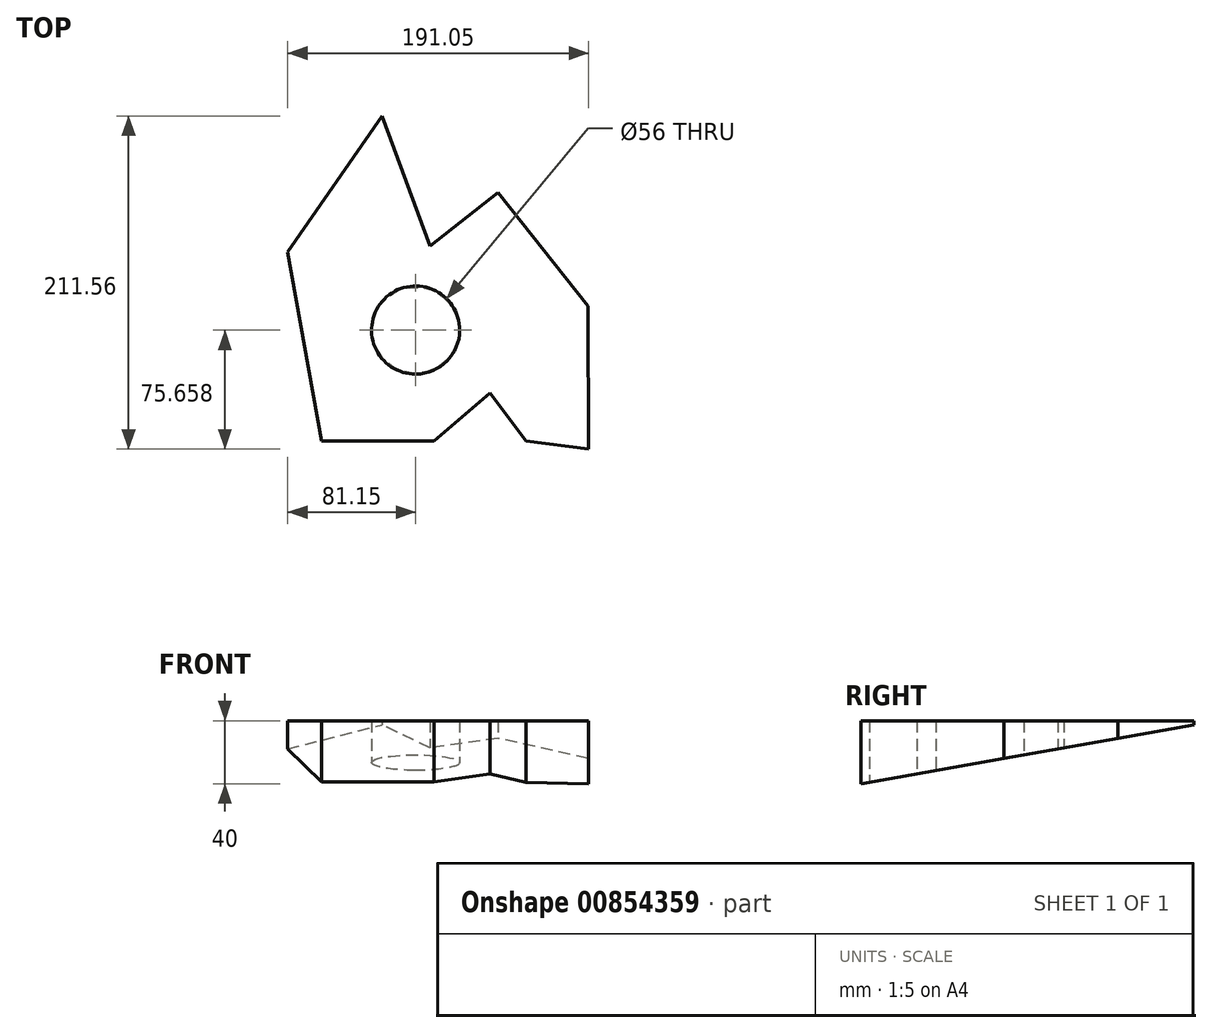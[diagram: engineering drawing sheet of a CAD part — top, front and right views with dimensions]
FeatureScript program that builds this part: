
annotation { "Feature Type Name" : "Feature", "Feature Type Description" : "" }
export const myFeature = defineFeature(function(context is Context, id is Id, definition is map)
    precondition{}
    {
        {
            var Q0;
            Q0=qCreatedBy(makeId("Top.planeOp"),FACE);
            var sketch = newSketch(context, id + "F0", { "sketchPlane" : qUnion([Q0])});
            skLineSegment(sketch, "E0", {"start": v(-21.43, 120.56) * mm, "end": v(-81.15, 34.2) * mm});
            skLineSegment(sketch, "E1", {"start": v(-21.43, 120.56) * mm, "end": v(9.15, 38.05) * mm});
            skLineSegment(sketch, "E2", {"start": v(9.15, 38.05) * mm, "end": v(52.3, 72.16) * mm});
            skLineSegment(sketch, "E3", {"start": v(52.3, 72.16) * mm, "end": v(109.36, 0) * mm});
            skLineSegment(sketch, "E4", {"start": v(109.36, 0) * mm, "end": v(109.9, -91) * mm});
            skLineSegment(sketch, "E5", {"start": v(109.9, -91) * mm, "end": v(70.25, -85.66) * mm});
            skLineSegment(sketch, "E6", {"start": v(70.25, -85.66) * mm, "end": v(47.2, -55.46) * mm});
            skLineSegment(sketch, "E7", {"start": v(47.2, -119.83) * mm, "end": v(-59.8, -119.83) * mm});
            skLineSegment(sketch, "E8", {"start": v(47.2, -55.46) * mm, "end": v(-5.77, -100.48) * mm});
            skLineSegment(sketch, "E9", {"start": v(11.65, -85.66) * mm, "end": v(-59.8, -85.66) * mm});
            skLineSegment(sketch, "E10", {"start": v(-59.8, -85.66) * mm, "end": v(-81.15, 34.2) * mm});
            skCircle(sketch, "E11", {"center": v(0, -15.34) * mm, "radius": 28 * mm});
            skSolve(sketch);
        }
        {
            var Q0;
            Q0=qSketchRegion(id+"F0",true);
            extrude(context, id + "F1", {"entities" : qUnion([Q0]), "depth" : 40 * mm, "offsetDistance" : 25 * mm});
        }
        {
            var Q0;
            Q0=makeQuery(id+"F1.opExtrude","SWEPT_FACE",FACE,{"disambiguationData":[OSD([sQuery(id+"F0.wireOp",EDGE,"E4")])]});
            var sketch = newSketch(context, id + "F2", { "sketchPlane" : qUnion([Q0])});
            skLineSegment(sketch, "E12", {"start": v(-91.64, 0) * mm, "end": v(-91.64, -37.54) * mm});
            skLineSegment(sketch, "E13", {"start": v(-91.64, 0) * mm, "end": v(-49.23, 7.48) * mm});
            skLineSegment(sketch, "E14.0.0", {"start": v(-0.64, 0) * mm, "end": v(71.85, 0) * mm});
            skLineSegment(sketch, "E14.0.1", {"start": v(71.85, 0) * mm, "end": v(71.85, 40) * mm});
            skLineSegment(sketch, "E14.0.2", {"start": v(71.85, 40) * mm, "end": v(-0.64, 40) * mm});
            skLineSegment(sketch, "E14.0.3", {"start": v(-0.64, 40) * mm, "end": v(-0.64, 0) * mm});
            skLineSegment(sketch, "E15", {"start": v(-91.64, 0) * mm, "end": v(71.85, 28.83) * mm});
            skLineSegment(sketch, "E16", {"start": v(71.85, 40) * mm, "end": v(160.51, 40) * mm});
            skLineSegment(sketch, "E17", {"start": v(-91.64, 0) * mm, "end": v(208.15, 52.86) * mm});
            skLineSegment(sketch, "E18", {"start": v(160.51, 40) * mm, "end": v(160.51, 0) * mm});
            skLineSegment(sketch, "E19", {"start": v(160.51, 0) * mm, "end": v(71.85, 0) * mm});
            skSolve(sketch);
        }
        {
            var Q0;
            {var subQ0=sQuery(id+"F2.wireOp",EDGE,"E18");Q0=makeQuery(id+"F2.imprint","IMPRINT",FACE,{"disambiguationData":[TD([[makeQuery(id+"F2.imprint","IMPRINT",EDGE,{"derivedFrom":subQ0}),-1.0]])]});}
            var Q1;
            {var subQ1=sQuery(id+"F0.wireOp",EDGE,"E4");var subQ2=makeQuery(id+"F1.opExtrude","CAP_EDGE",EDGE,{"disambiguationData":[OSD([subQ1])],"isStart":true});Q1=makeQuery(id+"F2.imprint","IMPRINT",FACE,{"disambiguationData":[TD([[makeQuery(id+"F2.imprint","IMPRINT",EDGE,{"derivedFrom":subQ2}),-1.0]])]});}
            var Q2;
            {var subQ0=sQuery(id+"F2.wireOp",EDGE,"E14.0.0");Q2=makeQuery(id+"F2.imprint","IMPRINT",FACE,{"disambiguationData":[TD([[makeQuery(id+"F2.imprint","IMPRINT",EDGE,{"derivedFrom":subQ0}),1.0]])]});}
            extrude(context, id + "F3", {"entities" : qUnion([Q0, Q1, Q2]), "operationType" : NewBodyOperationType.REMOVE, "oppositeDirection" : true, "depth" : 903 * mm, "offsetDistance" : 25 * mm});
        }
    });
